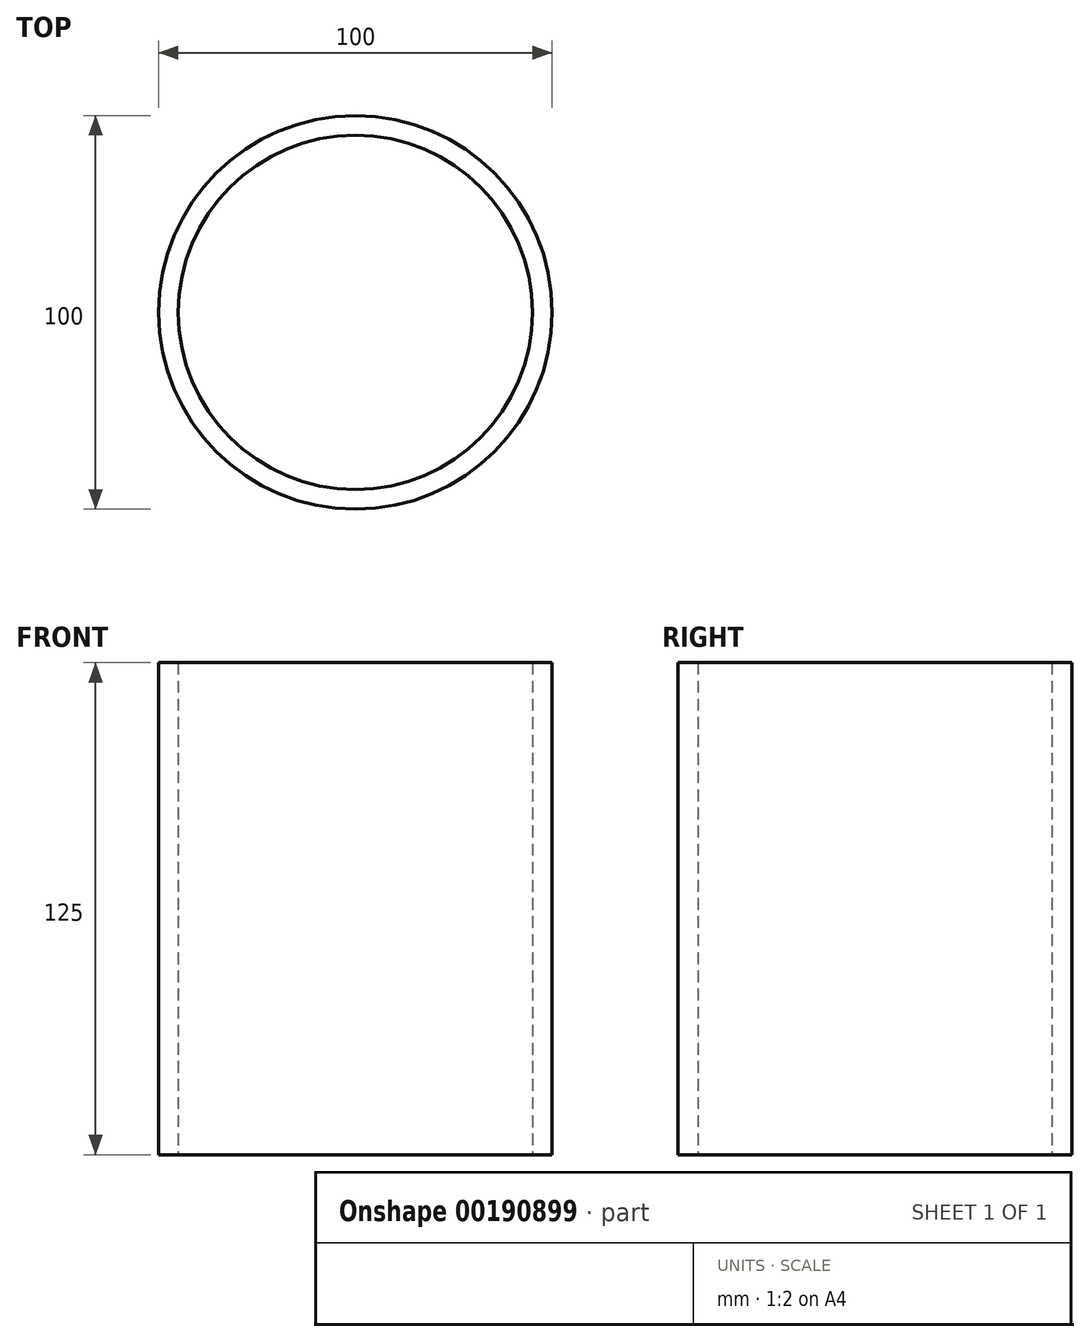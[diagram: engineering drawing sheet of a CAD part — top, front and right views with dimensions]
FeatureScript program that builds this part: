
annotation { "Feature Type Name" : "Feature", "Feature Type Description" : "" }
export const myFeature = defineFeature(function(context is Context, id is Id, definition is map)
    precondition{}
    {
        {
            var Q0;
            Q0=qCreatedBy(makeId("Top.planeOp"),FACE);
            var sketch = newSketch(context, id + "F0", { "sketchPlane" : qUnion([Q0])});
            skCircle(sketch, "E0", {"center": v(0, 0) * mm, "radius": 50 * mm});
            skSolve(sketch);
        }
        {
            var Q0;
            Q0 = qSketchRegion(id + "F0", true);
            extrude(context, id + "F1", {"entities" : qUnion([Q0]), "depth" : 125 * mm, "offsetDistance" : 25 * mm, "symmetric" : true});
        }
        {
            var Q0;
            Q0=makeQuery(id+"F1.opExtrude","CAP_FACE",FACE,{"disambiguationData":[OSD([sQuery(id+"F0.wireOp",EDGE,"E0")])],"isStart":false});
            var Q1;
            Q1=makeQuery(id+"F1.opExtrude","CAP_FACE",FACE,{"disambiguationData":[OSD([sQuery(id+"F0.wireOp",EDGE,"E0")])],"isStart":true});
            shell(context, id + "F2", {"entities" : qUnion([Q0, Q1]), "thickness" : 5 * mm});
        }
    });
